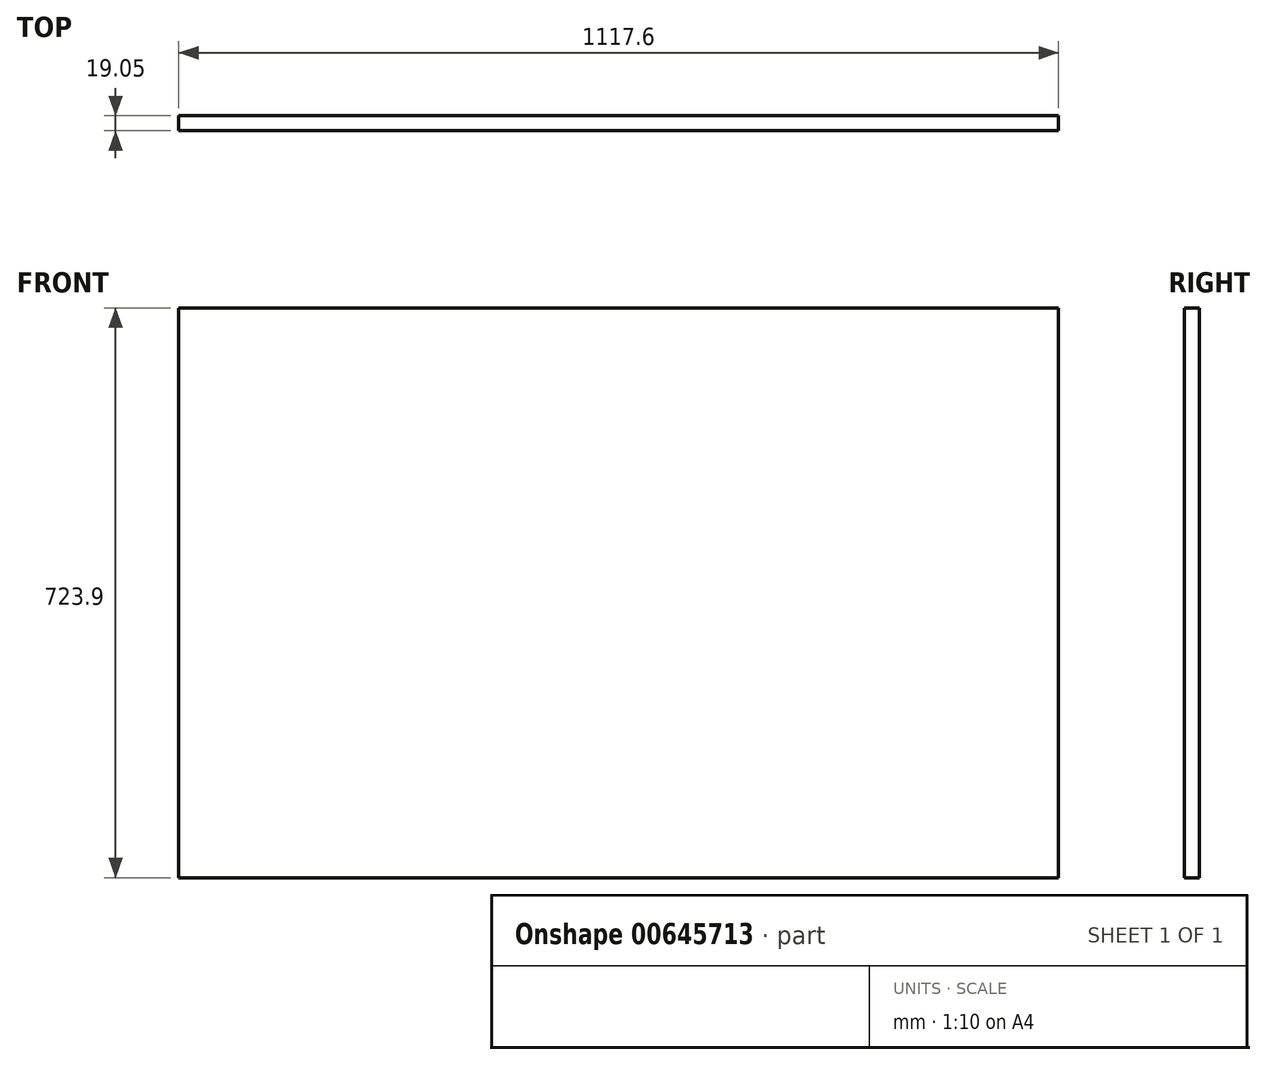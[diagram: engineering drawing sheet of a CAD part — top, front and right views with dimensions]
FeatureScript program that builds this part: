
annotation { "Feature Type Name" : "Feature", "Feature Type Description" : "" }
export const myFeature = defineFeature(function(context is Context, id is Id, definition is map)
    precondition{}
    {
        {
            var Q0;
            Q0=qCreatedBy(makeId("Front.planeOp"),FACE);
            var sketch = newSketch(context, id + "F0", { "sketchPlane" : qUnion([Q0])});
            skLineSegment(sketch, "E0.bottom", {"start": v(-558.8, 361.95) * mm, "end": v(558.8, 361.95) * mm});
            skLineSegment(sketch, "E0.top", {"start": v(-558.8, -361.95) * mm, "end": v(558.8, -361.95) * mm});
            skLineSegment(sketch, "E0.left", {"start": v(-558.8, 361.95) * mm, "end": v(-558.8, -361.95) * mm});
            skLineSegment(sketch, "E0.right", {"start": v(558.8, 361.95) * mm, "end": v(558.8, -361.95) * mm});
            skPoint(sketch, "E0.middle", {"position": v(0, 0) * mm});
            skSolve(sketch);
        }
        {
            var Q0;
            Q0=makeQuery(id+"F0.imprint","IMPRINT",FACE,{"disambiguationData":[TD([[makeQuery(id+"F0.imprint","IMPRINT",EDGE,{"derivedFrom":sQuery(id+"F0.wireOp",EDGE,"E0.bottom")}),-1.0]])]});
            extrude(context, id + "F1", {"entities" : qUnion([Q0]), "depth" : 19.05 * mm, "offsetDistance" : 25.4 * mm});
        }
    });
